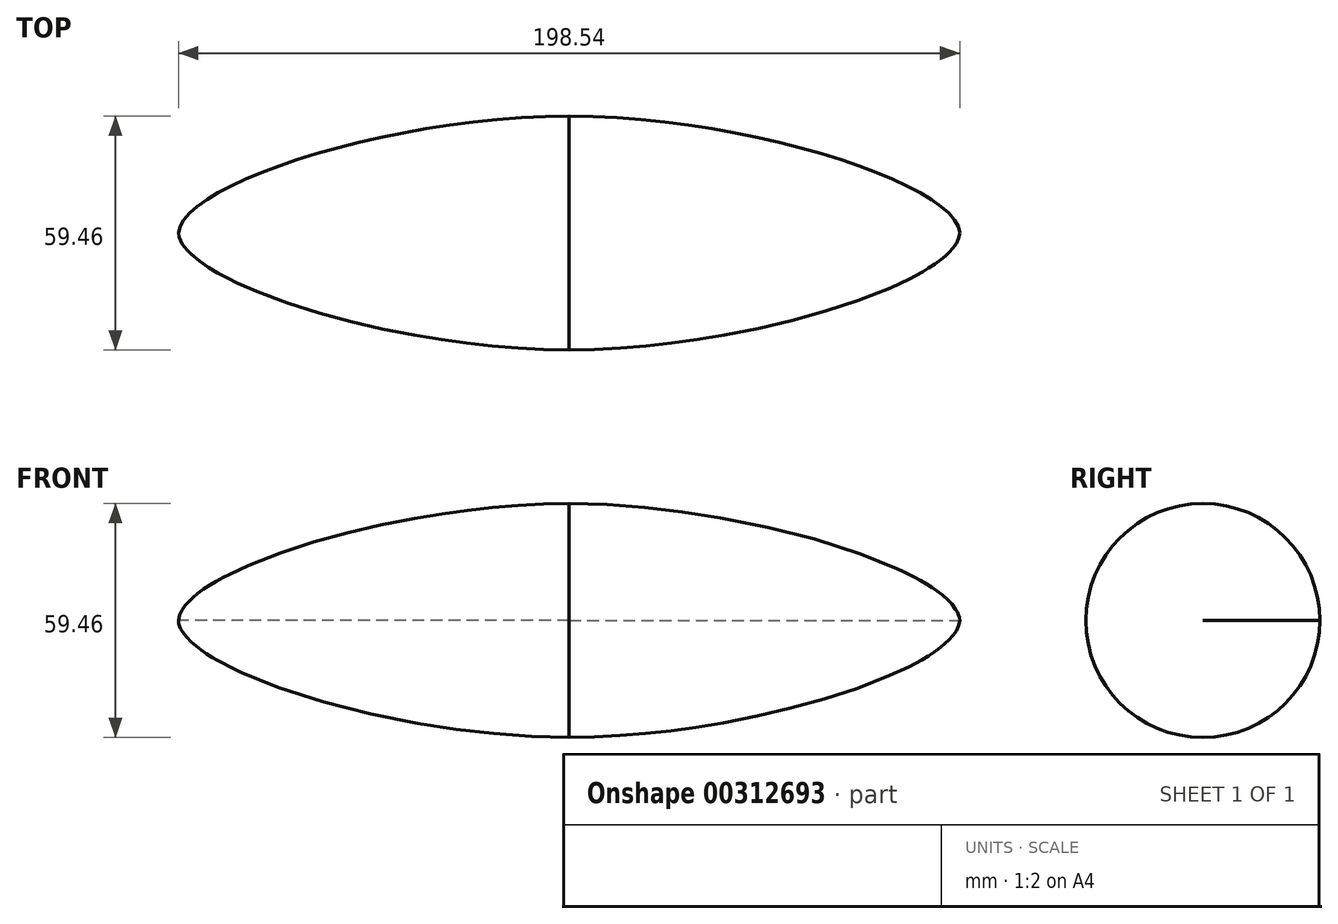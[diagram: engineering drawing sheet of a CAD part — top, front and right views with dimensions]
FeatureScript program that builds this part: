
annotation { "Feature Type Name" : "Feature", "Feature Type Description" : "" }
export const myFeature = defineFeature(function(context is Context, id is Id, definition is map)
    precondition{}
    {
        {
            var Q0;
            Q0=qCreatedBy(makeId("Right.planeOp"),FACE);
            var sketch = newSketch(context, id + "F0", { "sketchPlane" : qUnion([Q0])});
            skCircle(sketch, "E0", {"center": v(0, 0) * mm, "radius": 29.72 * mm});
            skLineSegment(sketch, "E1", {"start": v(0, 0) * mm, "end": v(29.72, 0) * mm});
            skLineSegment(sketch, "E2", {"start": v(0, 0) * mm, "end": v(-29.72, 0) * mm});
            skSolve(sketch);
        }
        {
            var Q0;
            Q0=qCreatedBy(makeId("Top.planeOp"),FACE);
            var sketch = newSketch(context, id + "F1", { "sketchPlane" : qUnion([Q0])});
            skLineSegment(sketch, "E3", {"start": v(0, 0) * mm, "end": v(-99.27, 0) * mm});
            skFitSpline(sketch, "E4", {"points": [v(0, 29.73) * mm, v(-99.27, 0) * mm, v(0, -29.72) * mm], "startDerivative": vector(-277.14, -1.48) * mm, "endDerivative": vector(297.8, -59.43) * mm});
            skLineSegment(sketch, "E5", {"start": v(-99.27, 0) * mm, "end": v(0, 0) * mm});
            skLineSegment(sketch, "E6", {"start": v(0, 0) * mm, "end": v(0, 29.73) * mm});
            skSolve(sketch);
        }
        {
            var Q0;
            Q0 = qSketchRegion(id + "F1", true);
            var Q1;
            Q1=sQuery(id+"F1.wireOp",EDGE,"E5");
            revolve(context, id + "F2", {"entities" : qUnion([Q0]), "axis" : qUnion([Q1]), "revolveType" : RevolveType.FULL});
        }
        {
            var Q0;
            Q0=makeQuery(id+"F2.opRevolve","SWEPT_BODY",BODY,{"disambiguationData":[OSD([sQuery(id+"F1.wireOp",EDGE,"E4"),sQuery(id+"F1.wireOp",EDGE,"E5"),sQuery(id+"F1.wireOp",EDGE,"E6")])]});
            var Q1;
            {var subQ0=sQuery(id+"F0.wireOp",EDGE,"E1");Q1=makeQuery(id+"F0.imprint","IMPRINT",FACE,{"disambiguationData":[TD([[makeQuery(id+"F0.imprint","IMPRINT",EDGE,{"derivedFrom":subQ0}),1.0]])]});}
            mirror(context, id + "F3", {"operationType" : NewBodyOperationType.ADD, "entities" : qUnion([Q0]), "mirrorPlane" : qUnion([Q1])});
        }
    });
